# Revit family: Interceptor_Grease_Extension-Zurn-GT2700-6-EXT
name_source: partatom
category: Plumbing Fixtures
units: mm (PartAtom-declared; Revit-internal decimal feet)

## family parameters
Always vertical = Yes
Cut with Voids When Loaded = No
Maintain Annotation Orientation = No
OmniClass Number = 23.45.30.00
OmniClass Title = Washing and Waste Disposal Equipment
Part Type = Normal
Room Calculation Point = No
Round Connector Dimension = Use Radius
Shared = No
Work Plane-Based = No

## types (10) — shared parameters
Assembly Code = D2090300
CW Connection = No
Default Elevation = 20 "
Description = GREASE TRAP EXTENSION
HW Connection = No
Main Material = Steel - Zurn  - A.R.E Coated
Manufacturer = Zurn Water, LLC
Manufacurer Brand = Zurn
Model = GT2700-6-EXT
Modified Date = 01/07/2026
Product Documentation Link = https://files.zurn.com
Product Page URL = https://www.zurn.com
Product data url = https://www.bimobject.com
URL = www.zurn.com
Vent Connection = No
WFU = 1
Waste Connection = Yes
zero-valued in all types: CWFU, HWFU

## per-type parameters (varying)
| type | Approx. Weight (Lbs) | Dimension "R" | Dimension "U" | Type Comments |
| JP2700-4-6 | 11 " | 13.25 " | 9.625 " | JP2700-4-6-EXT |
| JP2700-7-6 | 13 " | 14.625 " | 11.625 " | JP2700-7-6-EXT |
| JP2700-10-6 | 15 " | 16.625 " | 13.75 " | JP2700-10-6-EXT |
| JP2700-15-6 | 17 " | 18.625 " | 16.5 " | JP2700-15-6-EXT |
| JP2700-20-6 | 19 " | 21.5 " | 17 " | JP2700-20-6-EXT |
| JP2700-25-6 | 21 " | 23.5 " | 19.625 " | JP2700-25-6-EXT |
| JP2700-35-6 | 23 " | 23.375 " | 22.25 " | JP2700-35-6-EXT |
| JP2700-50-6 | 25 " | 27.25 " | 24.25 " | JP2700-50-6-EXT |
| JP2700-75-6 | 27 " | 32.25 " | 28.375 " | JP2700-75-6-EXT |
| JP2700-100-6 | 30 " | 36.25 " | 33.375 " | JP2700-100-6-EXT |

## geometry (parser evidence)
native form markers: Sweep x3
no freeform markers — native parametric forms only
